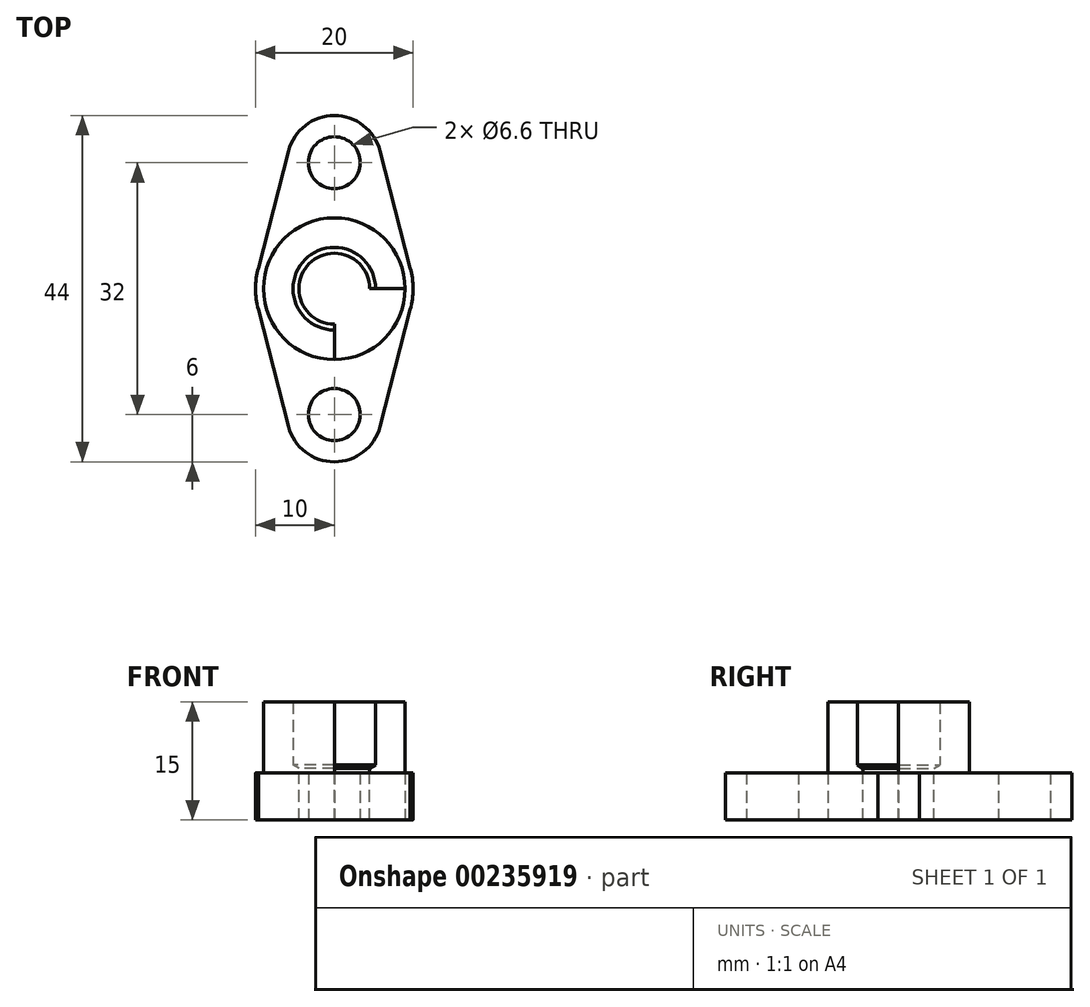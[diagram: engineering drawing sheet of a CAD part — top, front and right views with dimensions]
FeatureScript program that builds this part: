
annotation { "Feature Type Name" : "Feature", "Feature Type Description" : "" }
export const myFeature = defineFeature(function(context is Context, id is Id, definition is map)
    precondition{}
    {
        {
            var Q0;
            Q0=qCreatedBy(makeId("Top.planeOp"),FACE);
            var sketch = newSketch(context, id + "F0", { "sketchPlane" : qUnion([Q0])});
            skCircle(sketch, "E0", {"center": v(0, 0) * mm, "radius": 9 * mm});
            skArc(sketch, "E1", {"start": v(-9.65, 2.63) * mm, "mid": v(-10, 0) * mm, "end": v(-9.65, -2.63) * mm});
            skLineSegment(sketch, "E2", {"start": v(0, 0) * mm, "end": v(10, 0) * mm});
            skLineSegment(sketch, "E3", {"start": v(10, 0) * mm, "end": v(-10, 0) * mm});
            skLineSegment(sketch, "E4", {"start": v(0, 0) * mm, "end": v(0, -27.93) * mm});
            skLineSegment(sketch, "E5", {"start": v(0, -27.93) * mm, "end": v(0, 27.46) * mm});
            skCircle(sketch, "E6", {"center": v(0, 16) * mm, "radius": 3.3 * mm});
            skCircle(sketch, "E7.MirrorC", {"center": v(0, -16) * mm, "radius": 3.3 * mm});
            skArc(sketch, "E8", {"start": v(5.8, 17.5) * mm, "mid": v(0, 22) * mm, "end": v(-5.8, 17.5) * mm});
            skArc(sketch, "E9.MirrorC", {"start": v(5.8, -17.5) * mm, "mid": v(0, -22) * mm, "end": v(-5.8, -17.5) * mm});
            skLineSegment(sketch, "E10", {"start": v(-9.65, 2.63) * mm, "end": v(-5.8, 17.5) * mm});
            skLineSegment(sketch, "E11.MirrorCS", {"start": v(-9.65, -2.63) * mm, "end": v(-5.8, -17.5) * mm});
            skLineSegment(sketch, "E12.MirrorCS", {"start": v(9.65, 2.63) * mm, "end": v(5.8, 17.5) * mm});
            skLineSegment(sketch, "E13.MirrorCS", {"start": v(9.65, -2.63) * mm, "end": v(5.8, -17.5) * mm});
            skArc(sketch, "E14.trimOffspring", {"start": v(9.65, -2.63) * mm, "mid": v(10, 0) * mm, "end": v(9.65, 2.63) * mm});
            skSolve(sketch);
        }
        {
            var Q0;
            {var subQ10=sQuery(id+"F0.wireOp",EDGE,"E12.MirrorCS");Q0=makeQuery(id+"F0.imprint","IMPRINT",FACE,{"disambiguationData":[TD([[makeQuery(id+"F0.imprint","IMPRINT",EDGE,{"derivedFrom":subQ10}),1.0]])]});}
            var Q1;
            {var subQ5=sQuery(id+"F0.wireOp",EDGE,"E10");Q1=makeQuery(id+"F0.imprint","IMPRINT",FACE,{"disambiguationData":[TD([[makeQuery(id+"F0.imprint","IMPRINT",EDGE,{"derivedFrom":subQ5}),-1.0]])]});}
            var Q2;
            {var subQ11=sQuery(id+"F0.wireOp",EDGE,"E11.MirrorCS");Q2=makeQuery(id+"F0.imprint","IMPRINT",FACE,{"disambiguationData":[TD([[makeQuery(id+"F0.imprint","IMPRINT",EDGE,{"derivedFrom":subQ11}),1.0]])]});}
            var Q3;
            {var subQ12=sQuery(id+"F0.wireOp",EDGE,"E13.MirrorCS");Q3=makeQuery(id+"F0.imprint","IMPRINT",FACE,{"disambiguationData":[TD([[makeQuery(id+"F0.imprint","IMPRINT",EDGE,{"derivedFrom":subQ12}),-1.0]])]});}
            extrude(context, id + "F1", {"entities" : qUnion([Q0, Q1, Q2, Q3]), "depth" : 6 * mm});
        }
        {
            var Q0;
            {var subQ0=sQuery(id+"F0.wireOp",EDGE,"E3");var subQ1=sQuery(id+"F0.wireOp",EDGE,"E0");var subQ2=makeQuery(id+"F0.imprint","INTERSECT",VERTEX,{"disambiguationData":[OD(1.0)],"derivedFrom":[subQ1,subQ0]});Q0=makeQuery(id+"F0.imprint","IMPRINT",FACE,{"disambiguationData":[TD([[makeQuery(id+"F0.imprint","IMPRINT",EDGE,{"disambiguationData":[TD([[subQ2,-1.0]])],"derivedFrom":subQ1}),1.0]])]});}
            var Q1;
            {var subQ0=sQuery(id+"F0.wireOp",EDGE,"E5");var subQ1=sQuery(id+"F0.wireOp",EDGE,"E0");var subQ2=makeQuery(id+"F0.imprint","INTERSECT",VERTEX,{"disambiguationData":[OD(0.0)],"derivedFrom":[subQ1,subQ0]});Q1=makeQuery(id+"F0.imprint","IMPRINT",FACE,{"disambiguationData":[TD([[makeQuery(id+"F0.imprint","IMPRINT",EDGE,{"disambiguationData":[TD([[subQ2,-1.0]])],"derivedFrom":subQ1}),1.0]])]});}
            var Q2;
            {var subQ0=sQuery(id+"F0.wireOp",EDGE,"E5");var subQ1=sQuery(id+"F0.wireOp",EDGE,"E0");var subQ2=makeQuery(id+"F0.imprint","INTERSECT",VERTEX,{"disambiguationData":[OD(0.0)],"derivedFrom":[subQ1,subQ0]});Q2=makeQuery(id+"F0.imprint","IMPRINT",FACE,{"disambiguationData":[TD([[makeQuery(id+"F0.imprint","IMPRINT",EDGE,{"disambiguationData":[TD([[subQ2,1.0]])],"derivedFrom":subQ1}),1.0]])]});}
            var Q3;
            {var subQ0=sQuery(id+"F0.wireOp",EDGE,"E3");var subQ1=sQuery(id+"F0.wireOp",EDGE,"E0");var subQ2=makeQuery(id+"F0.imprint","INTERSECT",VERTEX,{"disambiguationData":[OD(0.0)],"derivedFrom":[subQ1,subQ0]});Q3=makeQuery(id+"F0.imprint","IMPRINT",FACE,{"disambiguationData":[TD([[makeQuery(id+"F0.imprint","IMPRINT",EDGE,{"disambiguationData":[TD([[subQ2,1.0]])],"derivedFrom":subQ1}),1.0]])]});}
            extrude(context, id + "F2", {"entities" : qUnion([Q0, Q1, Q2, Q3]), "operationType" : NewBodyOperationType.ADD, "depth" : 15 * mm});
        }
        {
            var Q0;
            Q0=qCreatedBy(makeId("Top.planeOp"),FACE);
            cPlane(context, id + "F3", {"entities" : qUnion([Q0]), "cplaneType" : CPlaneType.OFFSET, "offset" : 15 * mm, "width" : 150 * mm, "height" : 150 * mm});
        }
        {
            var Q0;
            Q0=qCreatedBy(id+"F3.planeOp",FACE);
            var sketch = newSketch(context, id + "F4", { "sketchPlane" : qUnion([Q0])});
            skCircle(sketch, "E15", {"center": v(0, 0) * mm, "radius": 4.5 * mm});
            skSolve(sketch);
        }
        {
            var Q0;
            Q0=sQuery(id+"F4.wireOp",VERTEX,"E15.center");
            var Q1;
            Q1=makeQuery(id+"F1.opExtrude","SWEPT_BODY",BODY,{"disambiguationData":[OSD([sQuery(id+"F0.wireOp",EDGE,"E0"),sQuery(id+"F0.wireOp",EDGE,"E1"),sQuery(id+"F0.wireOp",EDGE,"E6"),sQuery(id+"F0.wireOp",EDGE,"E7.MirrorC"),sQuery(id+"F0.wireOp",EDGE,"E8"),sQuery(id+"F0.wireOp",EDGE,"E9.MirrorC"),sQuery(id+"F0.wireOp",EDGE,"E10"),sQuery(id+"F0.wireOp",EDGE,"E11.MirrorCS"),sQuery(id+"F0.wireOp",EDGE,"E12.MirrorCS"),sQuery(id+"F0.wireOp",EDGE,"E13.MirrorCS"),sQuery(id+"F0.wireOp",EDGE,"E14.trimOffspring")])]});
            hole(context, id + "F5", {"style" : HoleStyle.SIMPLE, "endStyle" : HoleEndStyle.BLIND, "standardTappedOrClearance" : lookupTablePath({ "standard" : "ISO", "engagement" : "75%", "pitch" : "1.5 mm", "size" : "M12", "type" : "Tapped" }), "standardBlindInLast" : lookupTablePath({ "standard" : "ISO", "engagement" : "75%", "pitch" : "1.5 mm", "size" : "M12", "type" : "Tapped" }), "holeDiameter" : 10.5 * mm, "showTappedDepth" : true, "holeDepth" : 8 * mm, "tappedDepth" : 3.5 * mm, "tapClearance" : 3, "startFromSketch" : true, "locations" : qUnion([Q0]), "scope" : qUnion([Q1]), "majorDiameter" : 12 * mm});
        }
        {
            var Q0;
            Q0=sQuery(id+"F0.wireOp",VERTEX,"E1.center");
            var Q1;
            Q1=makeQuery(id+"F1.opExtrude","SWEPT_BODY",BODY,{"disambiguationData":[OSD([sQuery(id+"F0.wireOp",EDGE,"E0"),sQuery(id+"F0.wireOp",EDGE,"E1"),sQuery(id+"F0.wireOp",EDGE,"E6"),sQuery(id+"F0.wireOp",EDGE,"E7.MirrorC"),sQuery(id+"F0.wireOp",EDGE,"E8"),sQuery(id+"F0.wireOp",EDGE,"E9.MirrorC"),sQuery(id+"F0.wireOp",EDGE,"E10"),sQuery(id+"F0.wireOp",EDGE,"E11.MirrorCS"),sQuery(id+"F0.wireOp",EDGE,"E12.MirrorCS"),sQuery(id+"F0.wireOp",EDGE,"E13.MirrorCS"),sQuery(id+"F0.wireOp",EDGE,"E14.trimOffspring")])]});
            hole(context, id + "F6", {"style" : HoleStyle.SIMPLE, "endStyle" : HoleEndStyle.BLIND, "oppositeDirection" : true, "holeDiameter" : 9 * mm, "holeDepth" : 8 * mm, "tappedDepth" : 3.5 * mm, "tapClearance" : 3, "startFromSketch" : true, "locations" : qUnion([Q0]), "scope" : qUnion([Q1])});
        }
    });
